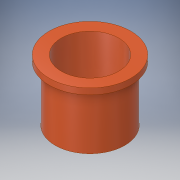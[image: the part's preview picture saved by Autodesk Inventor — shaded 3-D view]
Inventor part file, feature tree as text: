
AUTODESK INVENTOR PART (.ipt)
format: ipt  version: 2017 (Build 210142000, 142)  size: 145,920 bytes
history: native  units: in
note: dims shown in document units (in); Inventor stores cm internally (conversion verified against a paired STEP export)
features: revolve x1, sketch x1
ambient origin geometry x8: Origin, YZ Plane, XZ Plane, XY Plane, X Axis, Y Axis, Z Axis, Center Point
bodies: Body1 (feature_tree)
feature tree (2):
  revolve  "Revolution2"  [1 undecoded]
  sketch  "Sketch1"  dims[d0=0.25in d1=0.1718in d2=15.0deg d4=0.25in d5=1.5in d6=1.25in d7=0.25in d11=0.25in d13=0.5in d15=0.25in d16=0.25in d18=0.125in d19=0.5in d20=0.125in d21=0.25in d22=0.125in d23=0.125in d24=0.25in d25=0.5in d26=2.292in d27=0.5in d29=0.5in d30=90.0deg]
note: 1 required parameter value undecoded (feature->parameter linkage not recoverable at this tier; creation-order binding heuristic only, values carry confidence <= 0.55)
